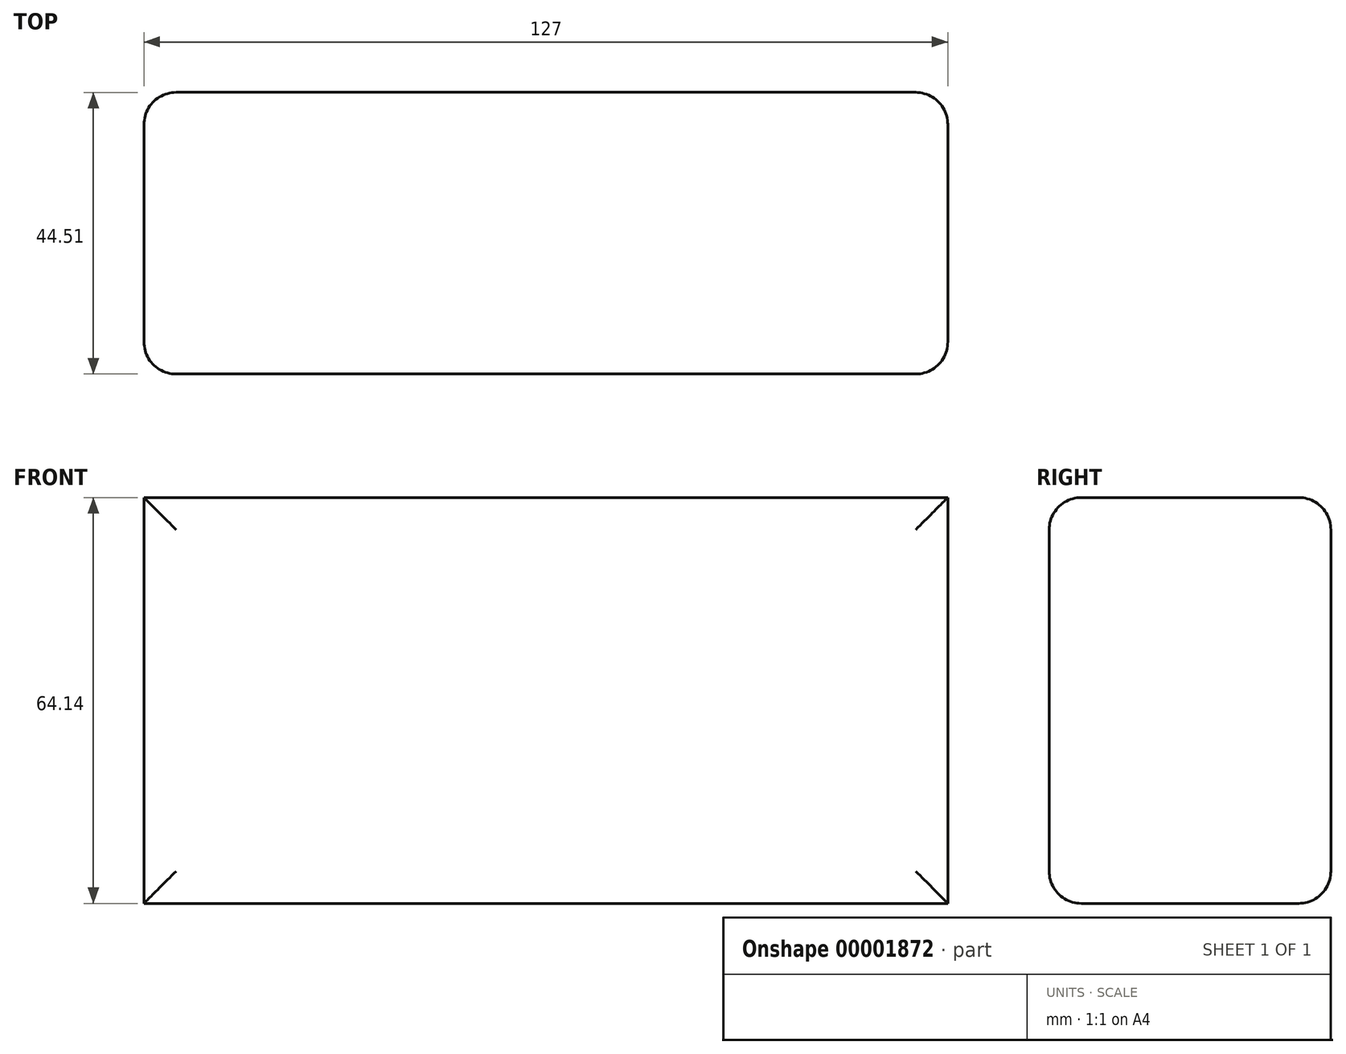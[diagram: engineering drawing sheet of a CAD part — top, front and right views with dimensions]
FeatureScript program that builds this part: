
annotation { "Feature Type Name" : "Feature", "Feature Type Description" : "" }
export const myFeature = defineFeature(function(context is Context, id is Id, definition is map)
    precondition{}
    {
        {
            var Q0;
            Q0=qCreatedBy(makeId("Top.planeOp"),FACE);
            var sketch = newSketch(context, id + "F0", { "sketchPlane" : qUnion([Q0])});
            skLineSegment(sketch, "E0.bottom", {"start": v(0, 0) * mm, "end": v(127, 0) * mm});
            skLineSegment(sketch, "E0.top", {"start": v(0, 44.51) * mm, "end": v(127, 44.51) * mm});
            skLineSegment(sketch, "E0.left", {"start": v(0, 0) * mm, "end": v(0, 44.51) * mm});
            skLineSegment(sketch, "E0.right", {"start": v(127, 0) * mm, "end": v(127, 44.51) * mm});
            skSolve(sketch);
        }
        {
            var Q0;
            Q0=makeQuery(id+"F0.imprint","IMPRINT",FACE,{"disambiguationData":[TD([[makeQuery(id+"F0.imprint","IMPRINT",EDGE,{"derivedFrom":sQuery(id+"F0.wireOp",EDGE,"E0.bottom")}),1.0]])]});
            extrude(context, id + "F1", {"entities" : qUnion([Q0]), "depth" : 64.14 * mm});
        }
        {
            var Q0;
            Q0=makeQuery(id+"F1.opExtrude","SWEPT_FACE",FACE,{"disambiguationData":[OSD([sQuery(id+"F0.wireOp",EDGE,"E0.bottom")])]});
            fillet(context, id + "F2", {"entities" : qUnion([Q0]), "radius" : 5.08 * mm, "tangentPropagation" : true, "allowEdgeOverflow" : false});
        }
        {
            var Q0;
            Q0=makeQuery(id+"F1.opExtrude","SWEPT_FACE",FACE,{"disambiguationData":[OSD([sQuery(id+"F0.wireOp",EDGE,"E0.top")])]});
            fillet(context, id + "F3", {"entities" : qUnion([Q0]), "radius" : 5.08 * mm, "tangentPropagation" : true, "allowEdgeOverflow" : false});
        }
    });
